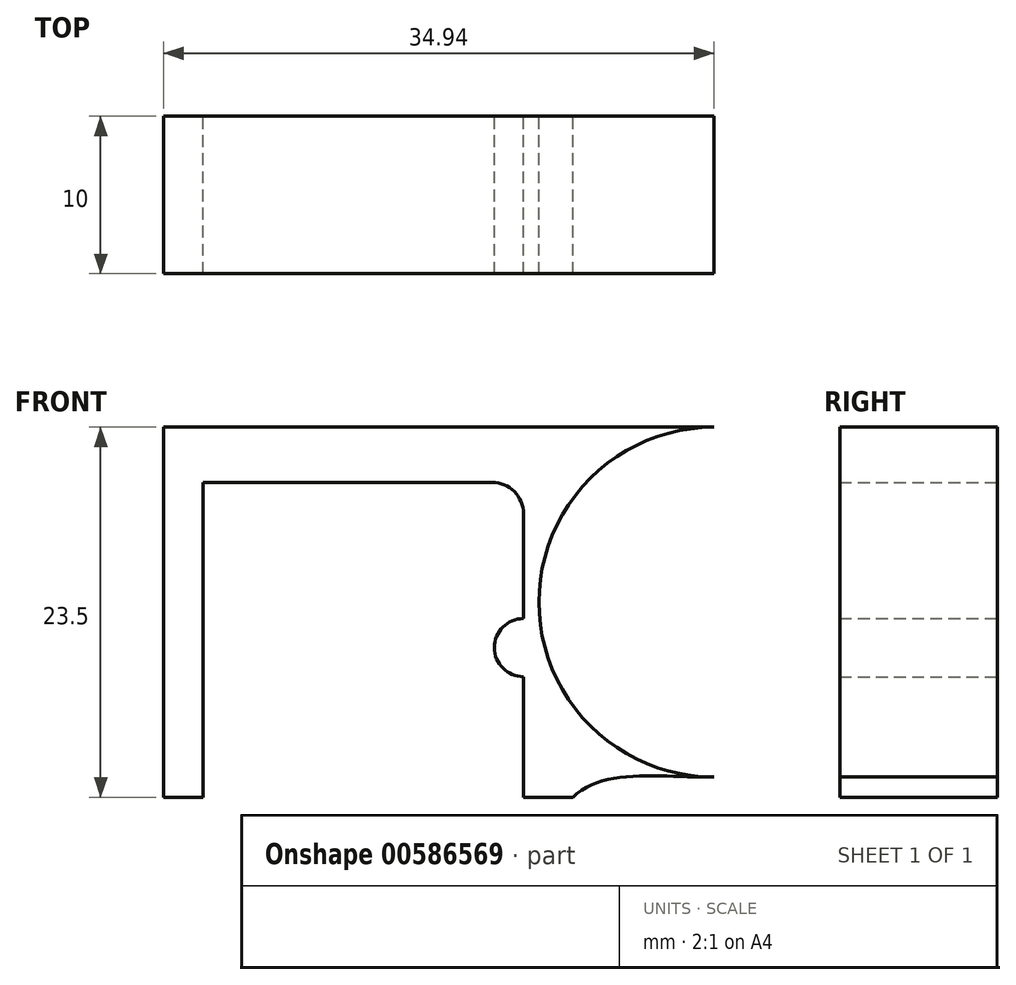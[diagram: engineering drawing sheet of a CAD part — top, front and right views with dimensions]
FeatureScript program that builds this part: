
annotation { "Feature Type Name" : "Feature", "Feature Type Description" : "" }
export const myFeature = defineFeature(function(context is Context, id is Id, definition is map)
    precondition{}
    {
        {
            var Q0;
            Q0=qCreatedBy(makeId("Front.planeOp"),FACE);
            var sketch = newSketch(context, id + "F0", { "sketchPlane" : qUnion([Q0])});
            skLineSegment(sketch, "E0", {"start": v(-50.57, 31.51) * mm, "end": v(-50.57, 8.01) * mm});
            skLineSegment(sketch, "E1", {"start": v(-50.57, 8.01) * mm, "end": v(-48.07, 8.01) * mm});
            skLineSegment(sketch, "E2", {"start": v(-48.07, 8.01) * mm, "end": v(-48.07, 28.01) * mm});
            skLineSegment(sketch, "E3", {"start": v(-48.07, 28.01) * mm, "end": v(-29.72, 28.01) * mm});
            skLineSegment(sketch, "E4", {"start": v(-27.72, 26.01) * mm, "end": v(-27.72, 8.01) * mm});
            skLineSegment(sketch, "E5", {"start": v(-27.72, 8.01) * mm, "end": v(-24.57, 8.01) * mm});
            skLineSegment(sketch, "E6", {"start": v(-24.57, 8.01) * mm, "end": v(-24.57, 31.51) * mm});
            skLineSegment(sketch, "E7", {"start": v(-24.57, 31.51) * mm, "end": v(-50.57, 31.51) * mm});
            skCircle(sketch, "E8", {"center": v(-15.63, 20.4) * mm, "radius": 9.28 * mm});
            skCircle(sketch, "E9", {"center": v(-15.63, 20.4) * mm, "radius": 11.1 * mm});
            skPoint(sketch, "E10.visualSharp", {"position": v(-27.72, 28.01) * mm});
            skArc(sketch, "E10.filletArc", {"start": v(-27.72, 26.01) * mm, "mid": v(-28.3, 27.42) * mm, "end": v(-29.72, 28.01) * mm});
            skPoint(sketch, "E11", {"position": v(-27.72, 17.51) * mm});
            skArc(sketch, "E12", {"start": v(-27.72, 19.36) * mm, "mid": v(-29.56, 17.51) * mm, "end": v(-27.72, 15.67) * mm});
            skLineSegment(sketch, "E13", {"start": v(-24.57, 31.51) * mm, "end": v(-15.63, 31.51) * mm});
            skFitSpline(sketch, "E14", {"points": [v(-24.57, 8.01) * mm, v(-15.63, 9.3) * mm], "startDerivative": vector(5.64, 5.79) * mm, "endDerivative": vector(9.34, 0.2) * mm});
            skSolve(sketch);
        }
        {
            var Q0;
            Q0=makeQuery(id+"F0.imprint","IMPRINT",FACE,{"disambiguationData":[TD([[makeQuery(id+"F0.imprint","IMPRINT",EDGE,{"derivedFrom":sQuery(id+"F0.wireOp",EDGE,"E0")}),1.0]])]});
            var Q1;
            {var subQ1=sQuery(id+"F0.wireOp",EDGE,"E6");var subQ4=sQuery(id+"F0.wireOp",EDGE,"E9");var subQ7=makeQuery(id+"F0.imprint","INTERSECT",VERTEX,{"disambiguationData":[OD(0.0)],"derivedFrom":[subQ1,subQ4]});Q1=makeQuery(id+"F0.imprint","IMPRINT",FACE,{"disambiguationData":[TD([[makeQuery(id+"F0.imprint","IMPRINT",EDGE,{"disambiguationData":[TD([[subQ7,-1.0]])],"derivedFrom":subQ1}),-1.0]])]});}
            var Q2;
            {var subQ0=sQuery(id+"F0.wireOp",EDGE,"E9");var subQ1=sQuery(id+"F0.wireOp",EDGE,"E6");var subQ2=makeQuery(id+"F0.imprint","INTERSECT",VERTEX,{"disambiguationData":[OD(0.0)],"derivedFrom":[subQ1,subQ0]});Q2=makeQuery(id+"F0.imprint","IMPRINT",FACE,{"disambiguationData":[TD([[makeQuery(id+"F0.imprint","IMPRINT",EDGE,{"disambiguationData":[TD([[subQ2,-1.0]])],"derivedFrom":subQ1}),1.0]])]});}
            var Q3;
            {var subQ0=sQuery(id+"F0.wireOp",EDGE,"E14");Q3=makeQuery(id+"F0.imprint","IMPRINT",FACE,{"disambiguationData":[TD([[makeQuery(id+"F0.imprint","IMPRINT",EDGE,{"derivedFrom":subQ0}),1.0]])]});}
            var Q4;
            {var subQ0=sQuery(id+"F0.wireOp",EDGE,"E12");Q4=makeQuery(id+"F0.imprint","IMPRINT",FACE,{"disambiguationData":[TD([[makeQuery(id+"F0.imprint","IMPRINT",EDGE,{"derivedFrom":subQ0}),1.0]])]});}
            var Q5;
            {var subQ0=sQuery(id+"F0.wireOp",EDGE,"E13");Q5=makeQuery(id+"F0.imprint","IMPRINT",FACE,{"disambiguationData":[TD([[makeQuery(id+"F0.imprint","IMPRINT",EDGE,{"derivedFrom":subQ0}),-1.0]])]});}
            extrude(context, id + "F1", {"entities" : qUnion([Q0, Q1, Q2, Q3, Q4, Q5]), "endBound" : BoundingType.SYMMETRIC, "depth" : 10 * mm, "offsetDistance" : 25 * mm});
        }
    });
